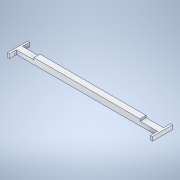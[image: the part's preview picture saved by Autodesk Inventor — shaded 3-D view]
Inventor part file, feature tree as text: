
AUTODESK INVENTOR PART (.ipt)
format: ipt  version: 2020.1 (Build 241239000, 239)  size: 133,120 bytes
history: native  units: mm
features: extrude x2, sketch x2, other x1
ambient origin geometry x8: Origin, YZ Plane, XZ Plane, XY Plane, X Axis, Y Axis, Z Axis, Center Point
bodies: Body1 (feature_tree)
feature tree (5):
  other  "Твердое тело1"
  extrude  "Выдавливание1"  Depth=30.0mm
  extrude  "Выдавливание2"  Depth=100.0mm
  sketch  "Эскиз1"
  sketch  "Эскиз2"
